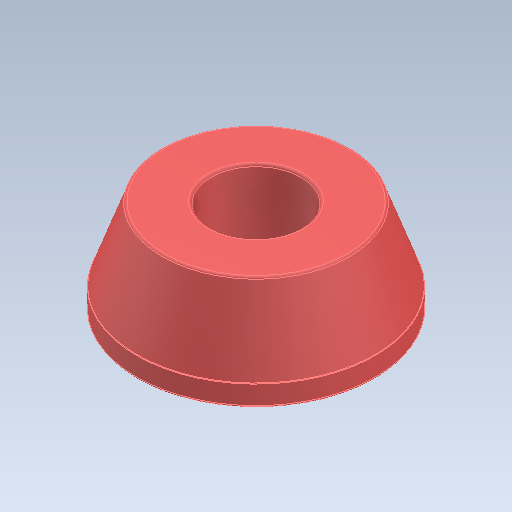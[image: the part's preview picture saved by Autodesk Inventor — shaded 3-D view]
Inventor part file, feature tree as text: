
AUTODESK INVENTOR PART (.ipt)
format: ipt  version: 2021 (Build 250183000, 183)  size: 143,872 bytes
history: mixed  units: in
note: dims shown in document units (in); Inventor stores cm internally (conversion verified against a paired STEP export)
features: fillet x1, imported_body x1
ambient origin geometry x8: Origin, YZ Plane, XZ Plane, XY Plane, X Axis, Y Axis, Z Axis, Center Point
bodies: Solid1 (imported_parasolid)
feature tree (2):
  fillet  "Fillet1"  [1 undecoded]
  imported_body  NMx_Import_Brep_tag  [imported B-rep: ~10 faces, bbox_mm=[0.0, 10.0, 25.0]]
note: 1 required parameter value undecoded (feature->parameter linkage not recoverable at this tier; creation-order binding heuristic only, values carry confidence <= 0.55)
